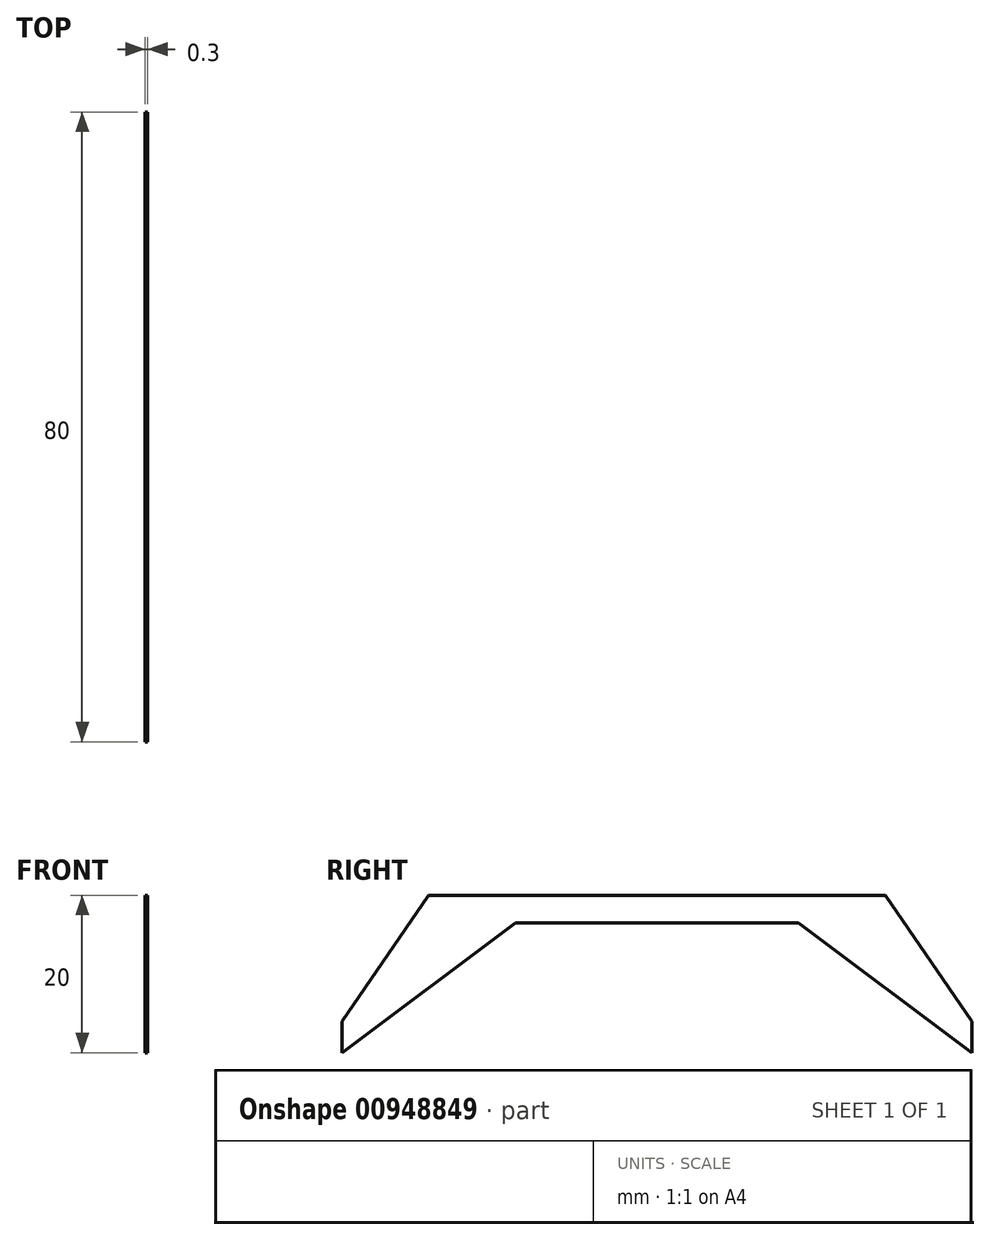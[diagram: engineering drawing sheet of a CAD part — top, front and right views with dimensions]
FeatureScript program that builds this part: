
annotation { "Feature Type Name" : "Feature", "Feature Type Description" : "" }
export const myFeature = defineFeature(function(context is Context, id is Id, definition is map)
    precondition{}
    {
        {
            var Q0;
            Q0=qCreatedBy(makeId("Right.planeOp"),FACE);
            var sketch = newSketch(context, id + "F0", { "sketchPlane" : qUnion([Q0])});
            skLineSegment(sketch, "E0.top", {"start": v(29, 10) * mm, "end": v(-29, 10) * mm});
            skLineSegment(sketch, "E0.left", {"start": v(40, -10) * mm, "end": v(40, -6) * mm});
            skLineSegment(sketch, "E0.right", {"start": v(-40, -10) * mm, "end": v(-40, -6) * mm});
            skPoint(sketch, "E0.middle", {"position": v(0, 0) * mm});
            skLineSegment(sketch, "E1", {"start": v(-40, -10) * mm, "end": v(-18, 6.5) * mm});
            skLineSegment(sketch, "E2", {"start": v(-18, 6.5) * mm, "end": v(18, 6.5) * mm});
            skLineSegment(sketch, "E3", {"start": v(18, 6.5) * mm, "end": v(40, -10) * mm});
            skLineSegment(sketch, "E4", {"start": v(-40, -6) * mm, "end": v(-29, 10) * mm});
            skLineSegment(sketch, "E5", {"start": v(40, -6) * mm, "end": v(29, 10) * mm});
            skPoint(sketch, "E6.orphan", {"position": v(-40, 10) * mm});
            skPoint(sketch, "E7.orphan", {"position": v(40, 10) * mm});
            skSolve(sketch);
        }
        {
            var Q0;
            Q0 = qSketchRegion(id + "F0", true);
            extrude(context, id + "F1", {"entities" : qUnion([Q0]), "depth" : 0.3 * mm, "offsetDistance" : 25 * mm});
        }
    });
